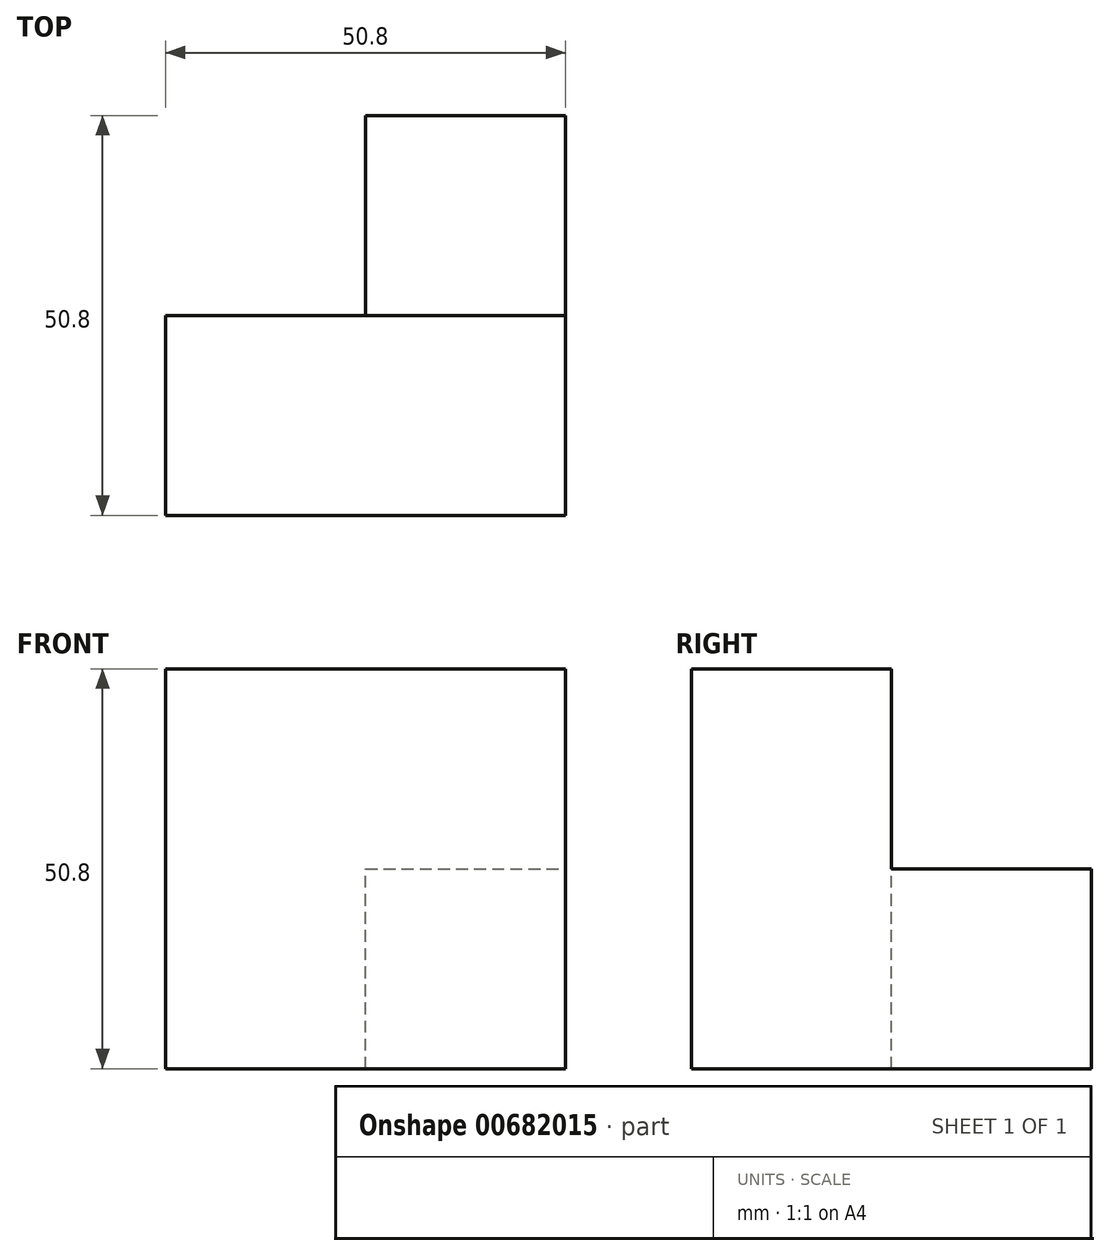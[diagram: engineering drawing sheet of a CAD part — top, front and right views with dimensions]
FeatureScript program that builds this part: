
annotation { "Feature Type Name" : "Feature", "Feature Type Description" : "" }
export const myFeature = defineFeature(function(context is Context, id is Id, definition is map)
    precondition{}
    {
        {
            var Q0;
            Q0=qCreatedBy(makeId("Front.planeOp"),FACE);
            var sketch = newSketch(context, id + "F0", { "sketchPlane" : qUnion([Q0])});
            skLineSegment(sketch, "E0", {"start": v(0, 0) * mm, "end": v(-50.8, 0) * mm});
            skLineSegment(sketch, "E1", {"start": v(-50.8, 0) * mm, "end": v(-50.8, 50.8) * mm});
            skLineSegment(sketch, "E2", {"start": v(-50.8, 50.8) * mm, "end": v(0, 50.8) * mm});
            skLineSegment(sketch, "E3", {"start": v(0, 50.8) * mm, "end": v(0, 0) * mm});
            skSolve(sketch);
        }
        {
            var Q0;
            Q0 = qSketchRegion(id + "F0", true);
            extrude(context, id + "F1", {"entities" : qUnion([Q0]), "depth" : 25.4 * mm, "offsetDistance" : 25.4 * mm});
        }
        {
            var Q0;
            Q0=qCreatedBy(makeId("Front.planeOp"),FACE);
            var sketch = newSketch(context, id + "F2", { "sketchPlane" : qUnion([Q0])});
            skLineSegment(sketch, "E4", {"start": v(0, 0) * mm, "end": v(-25.4, 0) * mm});
            skLineSegment(sketch, "E5", {"start": v(-25.4, 0) * mm, "end": v(-25.4, 25.4) * mm});
            skLineSegment(sketch, "E6", {"start": v(-25.4, 25.4) * mm, "end": v(0, 25.4) * mm});
            skLineSegment(sketch, "E7", {"start": v(0, 25.4) * mm, "end": v(0, 0) * mm});
            skSolve(sketch);
        }
        {
            var Q0;
            Q0 = qSketchRegion(id + "F2", true);
            extrude(context, id + "F3", {"entities" : qUnion([Q0]), "operationType" : NewBodyOperationType.ADD, "oppositeDirection" : true, "depth" : 25.4 * mm, "offsetDistance" : 25.4 * mm});
        }
    });
